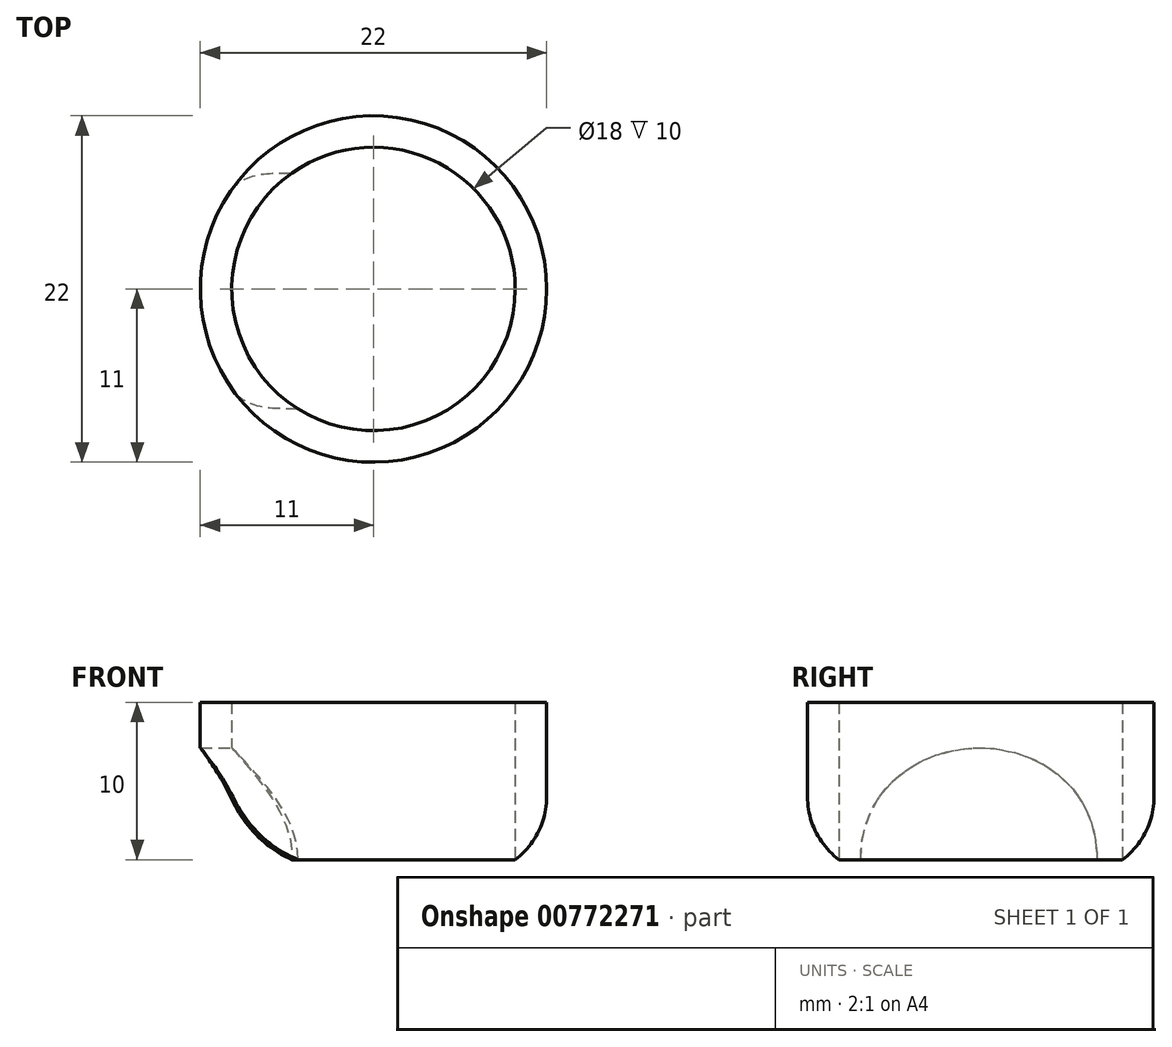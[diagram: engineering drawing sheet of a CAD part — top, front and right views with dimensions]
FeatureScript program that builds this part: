
annotation { "Feature Type Name" : "Feature", "Feature Type Description" : "" }
export const myFeature = defineFeature(function(context is Context, id is Id, definition is map)
    precondition{}
    {
        {
            var Q0;
            Q0=qCreatedBy(makeId("Top.planeOp"),FACE);
            var sketch = newSketch(context, id + "F0", { "sketchPlane" : qUnion([Q0])});
            skCircle(sketch, "E0", {"center": v(0, 0) * mm, "radius": 9 * mm});
            skArc(sketch, "E1", {"start": v(8.61, 6.85) * mm, "mid": v(6.35, 0) * mm, "end": v(8.61, -6.85) * mm});
            skArc(sketch, "E2", {"start": v(8.61, 6.85) * mm, "mid": v(-11, 0) * mm, "end": v(8.61, -6.85) * mm});
            skArc(sketch, "E3", {"start": v(8.61, -6.85) * mm, "mid": v(11, 0) * mm, "end": v(8.61, 6.85) * mm});
            skLineSegment(sketch, "E4", {"start": v(8.61, 6.85) * mm, "end": v(17.85, 0) * mm});
            skLineSegment(sketch, "E5", {"start": v(8.61, -6.85) * mm, "end": v(17.85, 0) * mm});
            skSolve(sketch);
        }
        {
            var Q0;
            Q0=makeQuery(id+"F0.imprint","IMPRINT",FACE,{"disambiguationData":[TD([[makeQuery(id+"F0.imprint","IMPRINT",EDGE,{"derivedFrom":sQuery(id+"F0.wireOp",EDGE,"E0")}),-1.0]])]});
            extrude(context, id + "F1", {"entities" : qUnion([Q0]), "depth" : 10 * mm, "offsetDistance" : 25 * mm});
        }
        {
            var Q0;
            Q0=qCreatedBy(makeId("Right.planeOp"),FACE);
            var sketch = newSketch(context, id + "F2", { "sketchPlane" : qUnion([Q0])});
            skFitSpline(sketch, "E6", {"points": [v(-7.63, 0) * mm, v(0, 7.1) * mm, v(7.37, 0) * mm], "startDerivative": vector(-0.02, 27.55) * mm, "endDerivative": vector(-0.23, -27.26) * mm});
            skLineSegment(sketch, "E7", {"start": v(-7.63, 0) * mm, "end": v(7.37, 0) * mm});
            skSolve(sketch);
        }
        {
            var Q0;
            Q0 = qSketchRegion(id + "F2", true);
            extrude(context, id + "F3", {"entities" : qUnion([Q0]), "operationType" : NewBodyOperationType.REMOVE, "oppositeDirection" : true, "depth" : 25 * mm, "offsetDistance" : 25 * mm});
        }
        {
            var Q0;
            Q0 = qSketchRegion(id + "F2", true);
            extrude(context, id + "F4", {"entities" : qUnion([Q0]), "operationType" : NewBodyOperationType.REMOVE, "oppositeDirection" : true, "depth" : 25 * mm, "offsetDistance" : 25 * mm});
        }
        {
            var Q0;
            Q0=makeQuery(id+"F1.opExtrude","CAP_EDGE",EDGE,{"disambiguationData":[OSD([sQuery(id+"F0.wireOp",EDGE,"E2"),sQuery(id+"F0.wireOp",EDGE,"E3")])],"isStart":true});
            fillet(context, id + "F5", {"entities" : qUnion([Q0]), "radius" : 5 * mm, "tangentPropagation" : true, "allowEdgeOverflow" : false});
        }
    });
